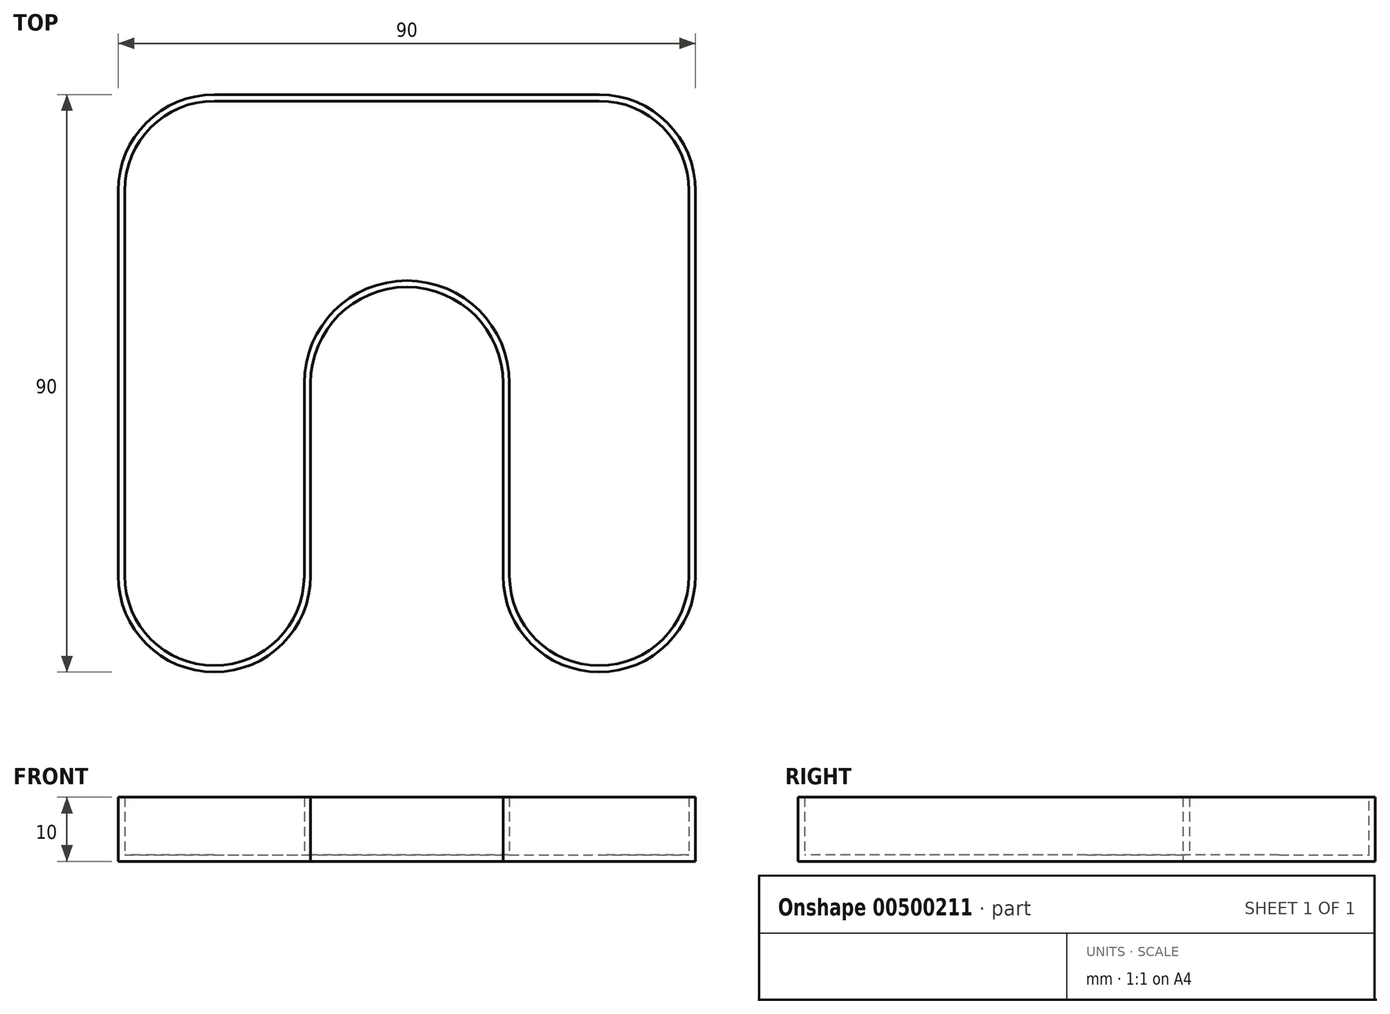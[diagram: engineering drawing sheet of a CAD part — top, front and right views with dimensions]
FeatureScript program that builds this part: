
annotation { "Feature Type Name" : "Feature", "Feature Type Description" : "" }
export const myFeature = defineFeature(function(context is Context, id is Id, definition is map)
    precondition{}
    {
        {
            var Q0;
            Q0=qCreatedBy(makeId("Top.planeOp"),FACE);
            var sketch = newSketch(context, id + "F0", { "sketchPlane" : qUnion([Q0])});
            skLineSegment(sketch, "E0.bottom", {"start": v(-26.26, 37.03) * mm, "end": v(33.74, 37.03) * mm});
            skLineSegment(sketch, "E0.top", {"start": v(-26.26, -52.97) * mm, "end": v(-26.26, -52.97) * mm});
            skLineSegment(sketch, "E0.left", {"start": v(-41.26, 22.03) * mm, "end": v(-41.26, -37.97) * mm});
            skLineSegment(sketch, "E0.right", {"start": v(48.74, 22.03) * mm, "end": v(48.74, -37.97) * mm});
            skLineSegment(sketch, "E1", {"start": v(18.74, -7.97) * mm, "end": v(18.74, -37.97) * mm});
            skLineSegment(sketch, "E2.trimOffspring", {"start": v(-11.26, -7.97) * mm, "end": v(-11.26, -37.97) * mm});
            skLineSegment(sketch, "E3.trimOffspring", {"start": v(3.74, 7.03) * mm, "end": v(3.74, 7.03) * mm});
            skLineSegment(sketch, "E4.trimOffspring", {"start": v(33.74, -52.97) * mm, "end": v(33.74, -52.97) * mm});
            skPoint(sketch, "E5.visualSharp", {"position": v(-41.26, -52.97) * mm});
            skArc(sketch, "E5.filletArc", {"start": v(-41.26, -37.97) * mm, "mid": v(-36.87, -48.58) * mm, "end": v(-26.26, -52.97) * mm});
            skPoint(sketch, "E6.visualSharp", {"position": v(-11.26, -52.97) * mm});
            skArc(sketch, "E6.filletArc", {"start": v(-26.26, -52.97) * mm, "mid": v(-15.65, -48.58) * mm, "end": v(-11.26, -37.97) * mm});
            skPoint(sketch, "E7.visualSharp", {"position": v(18.74, -52.97) * mm});
            skArc(sketch, "E7.filletArc", {"start": v(18.74, -37.97) * mm, "mid": v(23.13, -48.58) * mm, "end": v(33.74, -52.97) * mm});
            skPoint(sketch, "E8.visualSharp", {"position": v(48.74, -52.97) * mm});
            skArc(sketch, "E8.filletArc", {"start": v(33.74, -52.97) * mm, "mid": v(44.35, -48.58) * mm, "end": v(48.74, -37.97) * mm});
            skPoint(sketch, "E9.visualSharp", {"position": v(18.74, 7.03) * mm});
            skArc(sketch, "E9.filletArc", {"start": v(18.74, -7.97) * mm, "mid": v(14.35, 2.63) * mm, "end": v(3.74, 7.03) * mm});
            skPoint(sketch, "E10.visualSharp", {"position": v(-11.26, 7.03) * mm});
            skArc(sketch, "E10.filletArc", {"start": v(3.74, 7.03) * mm, "mid": v(-6.87, 2.63) * mm, "end": v(-11.26, -7.97) * mm});
            skPoint(sketch, "E11.visualSharp", {"position": v(48.74, 37.03) * mm});
            skArc(sketch, "E11.filletArc", {"start": v(48.74, 22.03) * mm, "mid": v(44.35, 32.63) * mm, "end": v(33.74, 37.03) * mm});
            skPoint(sketch, "E12.visualSharp", {"position": v(-41.26, 37.03) * mm});
            skArc(sketch, "E12.filletArc", {"start": v(-26.26, 37.03) * mm, "mid": v(-36.87, 32.63) * mm, "end": v(-41.26, 22.03) * mm});
            skSolve(sketch);
        }
        {
            var Q0;
            Q0 = qSketchRegion(id + "F0", true);
            extrude(context, id + "F1", {"entities" : qUnion([Q0]), "depth" : 10 * mm});
        }
        {
            var Q0;
            Q0=makeQuery(id+"F1.opExtrude","CAP_FACE",FACE,{"disambiguationData":[OSD([sQuery(id+"F0.wireOp",EDGE,"E0.bottom"),sQuery(id+"F0.wireOp",EDGE,"E0.left"),sQuery(id+"F0.wireOp",EDGE,"E0.right"),sQuery(id+"F0.wireOp",EDGE,"E1"),sQuery(id+"F0.wireOp",EDGE,"E2.trimOffspring"),sQuery(id+"F0.wireOp",EDGE,"E5.filletArc"),sQuery(id+"F0.wireOp",EDGE,"E6.filletArc"),sQuery(id+"F0.wireOp",EDGE,"E7.filletArc"),sQuery(id+"F0.wireOp",EDGE,"E8.filletArc"),sQuery(id+"F0.wireOp",EDGE,"E9.filletArc"),sQuery(id+"F0.wireOp",EDGE,"E10.filletArc"),sQuery(id+"F0.wireOp",EDGE,"E11.filletArc"),sQuery(id+"F0.wireOp",EDGE,"E12.filletArc")])],"isStart":false});
            shell(context, id + "F2", {"entities" : qUnion([Q0]), "thickness" : 1 * mm});
        }
    });
